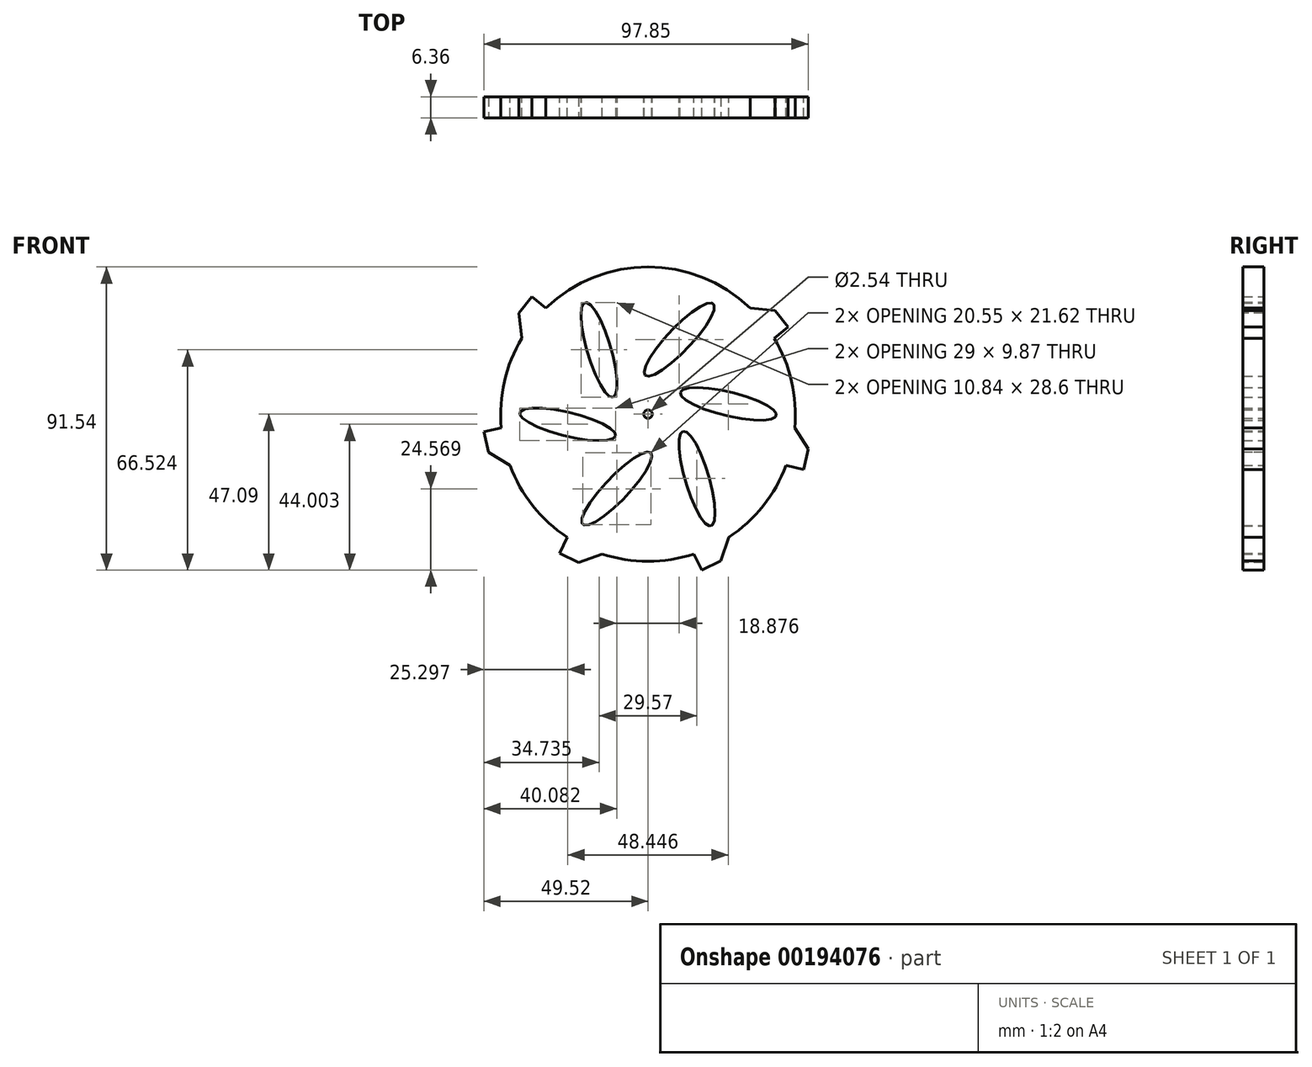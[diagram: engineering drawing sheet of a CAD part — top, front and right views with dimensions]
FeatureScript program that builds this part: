
annotation { "Feature Type Name" : "Feature", "Feature Type Description" : "" }
export const myFeature = defineFeature(function(context is Context, id is Id, definition is map)
    precondition{}
    {
        {
            var Q0;
            Q0=qCreatedBy(makeId("Front.planeOp"),FACE);
            var sketch = newSketch(context, id + "F0", { "sketchPlane" : qUnion([Q0])});
            skCircle(sketch, "E0", {"center": v(0, 0) * mm, "radius": 44.45 * mm});
            skCircle(sketch, "E1", {"center": v(0, 0) * mm, "radius": 1.27 * mm});
            skLineSegment(sketch, "E2.bottom", {"start": v(-5.83, 49.46) * mm, "end": v(5.83, 49.46) * mm});
            skLineSegment(sketch, "E2.left", {"start": v(-5.83, 49.46) * mm, "end": v(-5.83, 44.07) * mm});
            skLineSegment(sketch, "E2.right", {"start": v(5.83, 49.46) * mm, "end": v(5.83, 44.07) * mm});
            skPoint(sketch, "E2.middle", {"position": v(0, 44.45) * mm});
            skPoint(sketch, "E3.orphan", {"position": v(5.83, 39.44) * mm});
            skPoint(sketch, "E4.orphan", {"position": v(-5.83, 39.44) * mm});
            skLineSegment(sketch, "E5.1.0", {"start": v(35.04, 35.4) * mm, "end": v(42.3, 26.28) * mm});
            skLineSegment(sketch, "E5.1.1", {"start": v(42.3, 26.28) * mm, "end": v(38.09, 22.92) * mm});
            skLineSegment(sketch, "E5.1.2", {"start": v(35.04, 35.4) * mm, "end": v(30.82, 32.03) * mm});
            skLineSegment(sketch, "E5.2.0", {"start": v(49.52, -5.32) * mm, "end": v(46.93, -16.7) * mm});
            skLineSegment(sketch, "E5.2.1", {"start": v(46.93, -16.7) * mm, "end": v(41.66, -15.49) * mm});
            skLineSegment(sketch, "E5.2.2", {"start": v(49.52, -5.32) * mm, "end": v(44.26, -4.12) * mm});
            skLineSegment(sketch, "E5.3.0", {"start": v(26.71, -42.03) * mm, "end": v(16.2, -47.1) * mm});
            skLineSegment(sketch, "E5.3.1", {"start": v(16.2, -47.1) * mm, "end": v(13.87, -42.23) * mm});
            skLineSegment(sketch, "E5.3.2", {"start": v(26.71, -42.03) * mm, "end": v(24.37, -37.17) * mm});
            skLineSegment(sketch, "E5.4.0", {"start": v(-16.2, -47.1) * mm, "end": v(-26.71, -42.03) * mm});
            skLineSegment(sketch, "E5.4.1", {"start": v(-26.71, -42.03) * mm, "end": v(-24.37, -37.17) * mm});
            skLineSegment(sketch, "E5.4.2", {"start": v(-16.2, -47.1) * mm, "end": v(-13.87, -42.23) * mm});
            skLineSegment(sketch, "E5.5.0", {"start": v(-46.93, -16.7) * mm, "end": v(-49.52, -5.32) * mm});
            skLineSegment(sketch, "E5.5.1", {"start": v(-49.52, -5.32) * mm, "end": v(-44.26, -4.12) * mm});
            skLineSegment(sketch, "E5.5.2", {"start": v(-46.93, -16.7) * mm, "end": v(-41.66, -15.49) * mm});
            skLineSegment(sketch, "E5.6.0", {"start": v(-42.3, 26.28) * mm, "end": v(-35.04, 35.4) * mm});
            skLineSegment(sketch, "E5.6.1", {"start": v(-35.04, 35.4) * mm, "end": v(-30.82, 32.03) * mm});
            skLineSegment(sketch, "E5.6.2", {"start": v(-42.3, 26.28) * mm, "end": v(-38.09, 22.92) * mm});
            skLineSegment(sketch, "E5.anchor1", {"start": v(0, 0) * mm, "end": v(-5.83, 49.46) * mm, "construction": true});
            skLineSegment(sketch, "E5.anchor2", {"start": v(0, 0) * mm, "end": v(-5.83, 49.46) * mm, "construction": true});
            skEllipse(sketch, "E6", {"center": v(14.79, -19.43) * mm, "majorRadius": 14.91 * mm, "minorRadius": 3.58 * mm, "majorAxis": v(-0.28, 0.96)});
            skEllipse(sketch, "E7.1.0", {"center": v(24.22, 3.09) * mm, "majorRadius": 14.91 * mm, "minorRadius": 3.58 * mm, "majorAxis": v(-0.97, 0.23)});
            skEllipse(sketch, "E7.2.0", {"center": v(9.44, 22.52) * mm, "majorRadius": 14.91 * mm, "minorRadius": 3.58 * mm, "majorAxis": v(-0.69, -0.72)});
            skEllipse(sketch, "E7.3.0", {"center": v(-14.79, 19.43) * mm, "majorRadius": 14.91 * mm, "minorRadius": 3.58 * mm, "majorAxis": v(0.28, -0.96)});
            skEllipse(sketch, "E7.4.0", {"center": v(-24.22, -3.09) * mm, "majorRadius": 14.91 * mm, "minorRadius": 3.58 * mm, "majorAxis": v(0.97, -0.23)});
            skEllipse(sketch, "E7.5.0", {"center": v(-9.44, -22.52) * mm, "majorRadius": 14.91 * mm, "minorRadius": 3.58 * mm, "majorAxis": v(0.69, 0.72)});
            skSolve(sketch);
        }
        {
            var Q0;
            Q0=makeQuery(id+"F0.imprint","IMPRINT",FACE,{"disambiguationData":[TD([[makeQuery(id+"F0.imprint","IMPRINT",EDGE,{"derivedFrom":sQuery(id+"F0.wireOp",EDGE,"E1")}),-1.0]])]});
            var Q1;
            Q1=makeQuery(id+"F0.imprint","IMPRINT",FACE,{"disambiguationData":[TD([[makeQuery(id+"F0.imprint","IMPRINT",EDGE,{"derivedFrom":sQuery(id+"F0.wireOp",EDGE,"E5.6.0")}),-1.0]])]});
            var Q2;
            Q2=makeQuery(id+"F0.imprint","IMPRINT",FACE,{"disambiguationData":[TD([[makeQuery(id+"F0.imprint","IMPRINT",EDGE,{"derivedFrom":sQuery(id+"F0.wireOp",EDGE,"E2.bottom")}),-1.0]])]});
            var Q3;
            Q3=makeQuery(id+"F0.imprint","IMPRINT",FACE,{"disambiguationData":[TD([[makeQuery(id+"F0.imprint","IMPRINT",EDGE,{"derivedFrom":sQuery(id+"F0.wireOp",EDGE,"E5.1.0")}),-1.0]])]});
            var Q4;
            Q4=makeQuery(id+"F0.imprint","IMPRINT",FACE,{"disambiguationData":[TD([[makeQuery(id+"F0.imprint","IMPRINT",EDGE,{"derivedFrom":sQuery(id+"F0.wireOp",EDGE,"E5.2.0")}),-1.0]])]});
            var Q5;
            Q5=makeQuery(id+"F0.imprint","IMPRINT",FACE,{"disambiguationData":[TD([[makeQuery(id+"F0.imprint","IMPRINT",EDGE,{"derivedFrom":sQuery(id+"F0.wireOp",EDGE,"E5.3.0")}),-1.0]])]});
            var Q6;
            Q6=makeQuery(id+"F0.imprint","IMPRINT",FACE,{"disambiguationData":[TD([[makeQuery(id+"F0.imprint","IMPRINT",EDGE,{"derivedFrom":sQuery(id+"F0.wireOp",EDGE,"E5.4.0")}),-1.0]])]});
            var Q7;
            Q7=makeQuery(id+"F0.imprint","IMPRINT",FACE,{"disambiguationData":[TD([[makeQuery(id+"F0.imprint","IMPRINT",EDGE,{"derivedFrom":sQuery(id+"F0.wireOp",EDGE,"E5.5.0")}),-1.0]])]});
            extrude(context, id + "F1", {"entities" : qUnion([Q0, Q1, Q2, Q3, Q4, Q5, Q6, Q7]), "endBound" : BoundingType.SYMMETRIC, "depth" : 6.35 * mm});
        }
        {
            var Q0;
            Q0=makeQuery(id+"F1.opExtrude","SWEPT_EDGE",EDGE,{"disambiguationData":[OSD([sQuery(id+"F0.wireOp",EDGE,"E5.6.0"),sQuery(id+"F0.wireOp",EDGE,"E5.6.2")])]});
            var Q1;
            Q1=makeQuery(id+"F1.opExtrude","SWEPT_EDGE",EDGE,{"disambiguationData":[OSD([sQuery(id+"F0.wireOp",EDGE,"E5.5.0"),sQuery(id+"F0.wireOp",EDGE,"E5.5.2")])]});
            var Q2;
            Q2=makeQuery(id+"F1.opExtrude","SWEPT_EDGE",EDGE,{"disambiguationData":[OSD([sQuery(id+"F0.wireOp",EDGE,"E2.bottom"),sQuery(id+"F0.wireOp",EDGE,"E2.left")])]});
            var Q3;
            Q3=makeQuery(id+"F1.opExtrude","SWEPT_EDGE",EDGE,{"disambiguationData":[OSD([sQuery(id+"F0.wireOp",EDGE,"E5.1.0"),sQuery(id+"F0.wireOp",EDGE,"E5.1.2")])]});
            var Q4;
            Q4=makeQuery(id+"F1.opExtrude","SWEPT_EDGE",EDGE,{"disambiguationData":[OSD([sQuery(id+"F0.wireOp",EDGE,"E5.2.0"),sQuery(id+"F0.wireOp",EDGE,"E5.2.2")])]});
            var Q5;
            Q5=makeQuery(id+"F1.opExtrude","SWEPT_EDGE",EDGE,{"disambiguationData":[OSD([sQuery(id+"F0.wireOp",EDGE,"E5.3.0"),sQuery(id+"F0.wireOp",EDGE,"E5.3.2")])]});
            var Q6;
            Q6=makeQuery(id+"F1.opExtrude","SWEPT_EDGE",EDGE,{"disambiguationData":[OSD([sQuery(id+"F0.wireOp",EDGE,"E5.4.0"),sQuery(id+"F0.wireOp",EDGE,"E5.4.2")])]});
            chamfer(context, id + "F2", {"entities" : qUnion([Q0, Q1, Q2, Q3, Q4, Q5, Q6]), "width" : 5.33 * mm, "tangentPropagation" : true});
        }
    });
